FCSTD DOCUMENT  (FreeCAD 0.15R4671 (Git))
Label: Sixth Motor Frame 2
License: All rights reserved
LicenseURL: http://en.wikipedia.org/wiki/All_rights_reserved
objects: Sketcher::SketchObject×1
note: 1 computed .brp shape members not serialized (recipe doc carries the construction recipe); baked Part::Feature solids carry a one-line shape summary decoded from their .brp

FEATURE [Sketcher::SketchObject] Sketch
  sketch-geometry (4):
    g0: LineSegment StartX=-63.5 StartY=23 StartZ=0 EndX=63.5 EndY=23 EndZ=0
    g1: LineSegment StartX=63.5 StartY=23 StartZ=0 EndX=63.5 EndY=-23 EndZ=0
    g2: LineSegment StartX=63.5 StartY=-23 StartZ=0 EndX=-63.5 EndY=-23 EndZ=0
    g3: LineSegment StartX=-63.5 StartY=-23 StartZ=0 EndX=-63.5 EndY=23 EndZ=0
  constraints (12):
    c: Coincident(g0,g1)
    c: Coincident(g1,g2)
    c: Coincident(g2,g3)
    c: Coincident(g3,g0)
    c: Horizontal(g0)
    c: Horizontal(g2)
    c: Vertical(g1)
    c: Vertical(g3)
    c: Symmetric(g0,g2,g-1)
    c: Symmetric(g0,g0,g-2)
    c: Distance(g3) = 46
    c: Distance(g0) = 127
